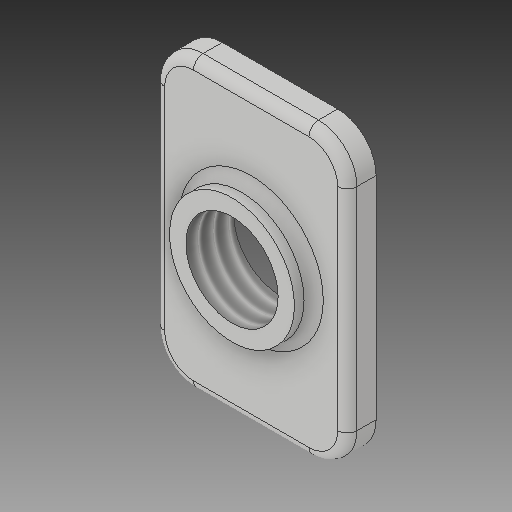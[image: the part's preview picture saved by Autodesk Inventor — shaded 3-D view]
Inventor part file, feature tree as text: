
AUTODESK INVENTOR PART (.ipt)
format: ipt  version: 2018 (Build 220112000, 112)  size: 177,664 bytes
history: native  units: mm
features: other x3, sketch x2
ambient origin geometry x8: Origin, YZ Plane, XZ Plane, XY Plane, X Axis, Y Axis, Z Axis, Center Point
bodies: Solid1 (feature_tree)
feature tree (5):
  other  "M5 Tee Nut-Generic_MIR.ipt"
  other  "Solid1::M5 Tee Nut-Generic_MIR.ipt"
  other  "TaggingFeature1"
  sketch  "Sketch1"  dims[d0=10.0mm]
  sketch  "Sketch2"
